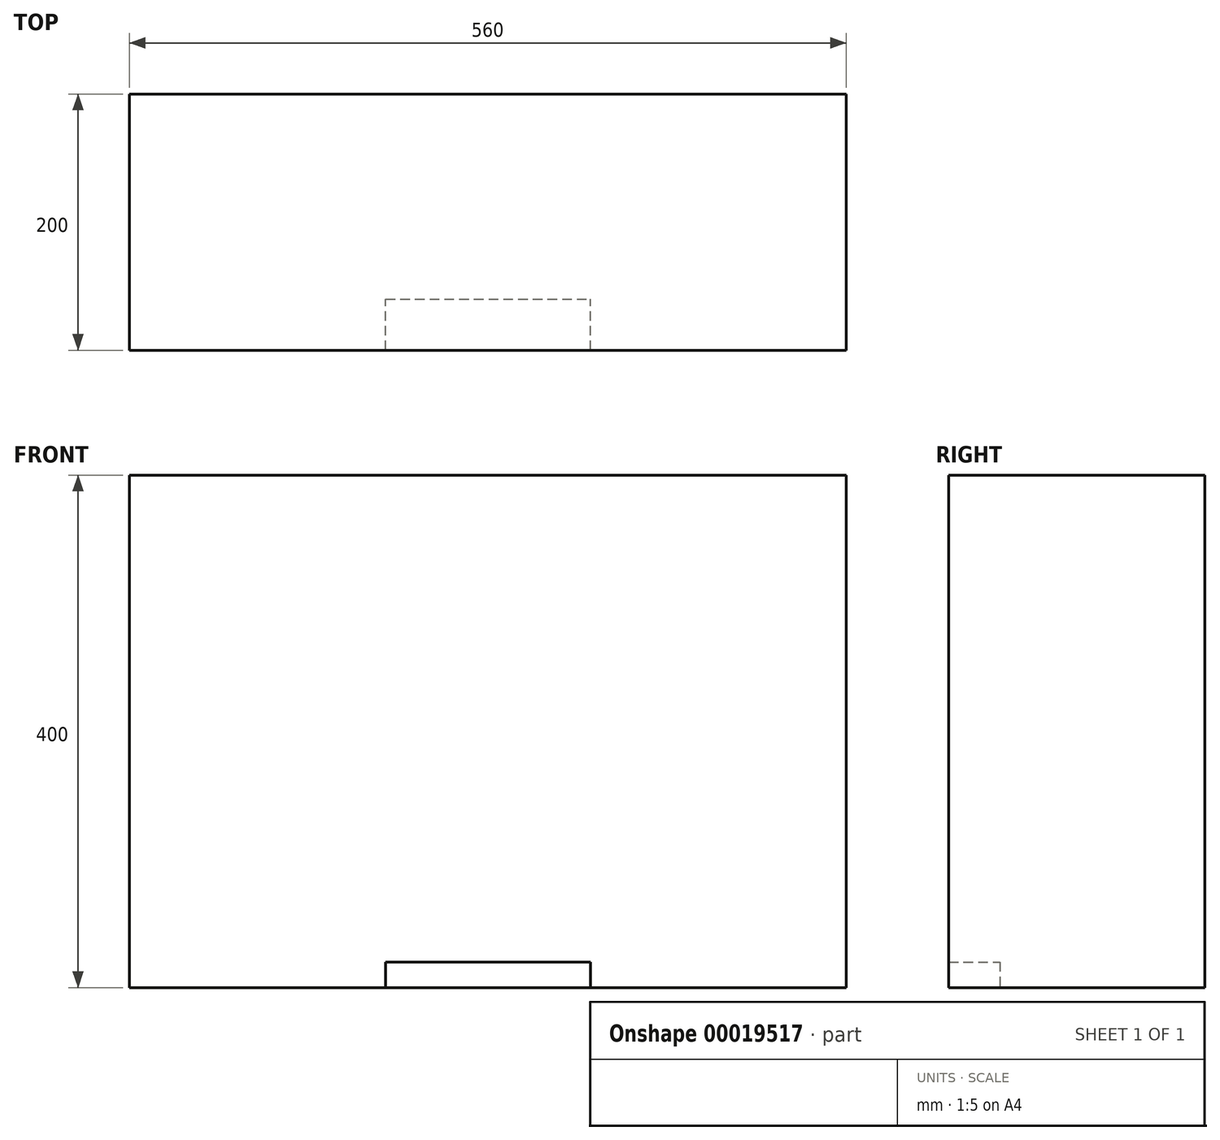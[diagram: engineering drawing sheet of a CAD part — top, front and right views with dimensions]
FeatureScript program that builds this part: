
annotation { "Feature Type Name" : "Feature", "Feature Type Description" : "" }
export const myFeature = defineFeature(function(context is Context, id is Id, definition is map)
    precondition{}
    {
        {
            var Q0;
            Q0=qCreatedBy(makeId("Top.planeOp"),FACE);
            var sketch = newSketch(context, id + "F0", { "sketchPlane" : qUnion([Q0])});
            skLineSegment(sketch, "E0.bottom", {"start": v(-280, 200) * mm, "end": v(0, 200) * mm});
            skLineSegment(sketch, "E0.top", {"start": v(-280, 0) * mm, "end": v(0, 0) * mm});
            skLineSegment(sketch, "E0.left", {"start": v(-280, 200) * mm, "end": v(-280, 0) * mm});
            skLineSegment(sketch, "E0.right", {"start": v(0, 200) * mm, "end": v(0, 0) * mm});
            skLineSegment(sketch, "E1.bottom", {"start": v(0, 0) * mm, "end": v(280, 0) * mm});
            skLineSegment(sketch, "E1.top", {"start": v(0, 200) * mm, "end": v(280, 200) * mm});
            skLineSegment(sketch, "E1.left", {"start": v(0, 0) * mm, "end": v(0, 200) * mm});
            skLineSegment(sketch, "E1.right", {"start": v(280, 0) * mm, "end": v(280, 200) * mm});
            skSolve(sketch);
        }
        {
            var Q0;
            Q0=makeQuery(id+"F0.imprint","IMPRINT",FACE,{"disambiguationData":[TD([[makeQuery(id+"F0.imprint","IMPRINT",EDGE,{"derivedFrom":sQuery(id+"F0.wireOp",EDGE,"E0.bottom")}),-1.0]])]});
            var Q1;
            Q1=makeQuery(id+"F0.imprint","IMPRINT",FACE,{"disambiguationData":[TD([[makeQuery(id+"F0.imprint","IMPRINT",EDGE,{"derivedFrom":sQuery(id+"F0.wireOp",EDGE,"E1.bottom")}),1.0]])]});
            extrude(context, id + "F1", {"entities" : qUnion([Q0, Q1]), "depth" : 400 * mm});
        }
        {
            var Q0;
            Q0=makeQuery(id+"F1.opExtrude","CAP_FACE",FACE,{"disambiguationData":[OSD([sQuery(id+"F0.wireOp",EDGE,"E0.bottom"),sQuery(id+"F0.wireOp",EDGE,"E0.top"),sQuery(id+"F0.wireOp",EDGE,"E0.left"),sQuery(id+"F0.wireOp",EDGE,"E0.right")])],"isStart":true});
            var sketch = newSketch(context, id + "F2", { "sketchPlane" : qUnion([Q0])});
            skLineSegment(sketch, "E2.bottom", {"start": v(-79.85, 0) * mm, "end": v(80.15, 0) * mm});
            skLineSegment(sketch, "E2.top", {"start": v(-79.85, -40) * mm, "end": v(80.15, -40) * mm});
            skLineSegment(sketch, "E2.left", {"start": v(-79.85, 0) * mm, "end": v(-79.85, -40) * mm});
            skLineSegment(sketch, "E2.right", {"start": v(80.15, 0) * mm, "end": v(80.15, -40) * mm});
            skSolve(sketch);
        }
        {
            var Q0;
            Q0 = qSketchRegion(id + "F2", true);
            extrude(context, id + "F3", {"entities" : qUnion([Q0]), "operationType" : NewBodyOperationType.REMOVE, "oppositeDirection" : true, "depth" : 20 * mm});
        }
    });
